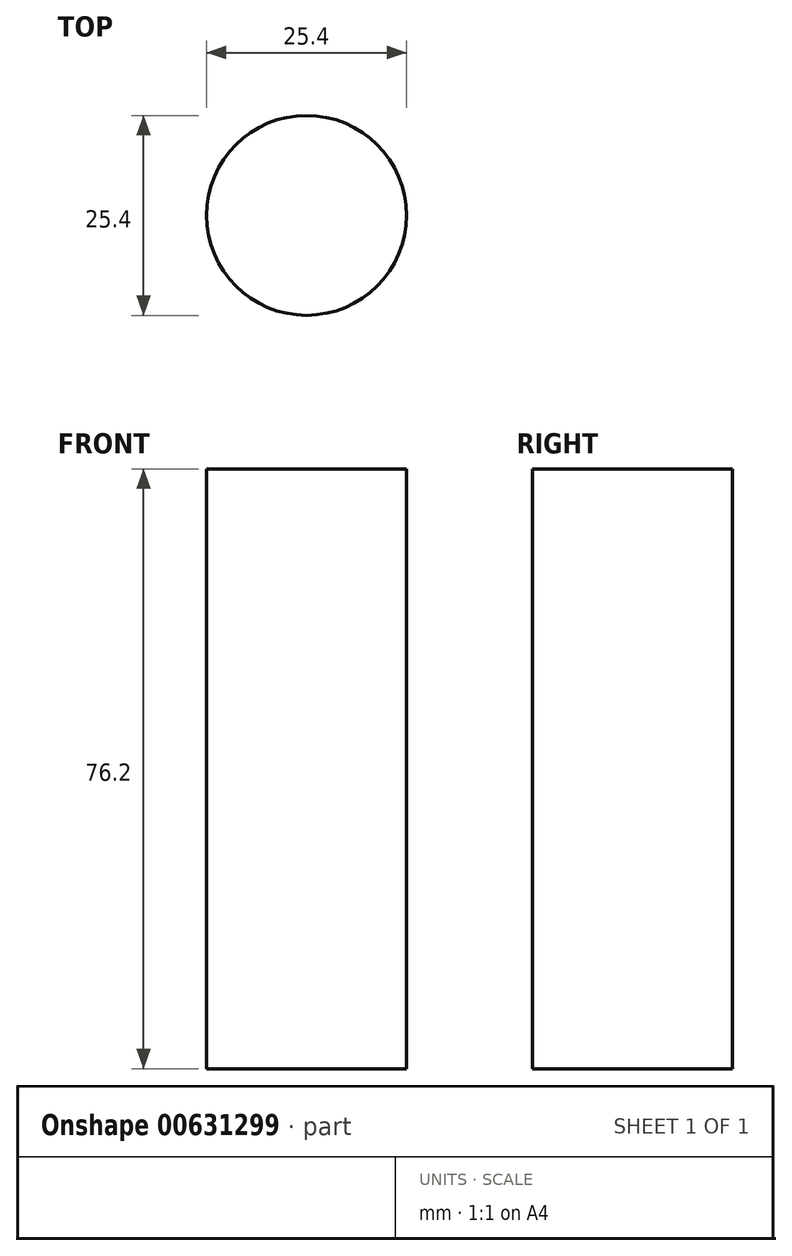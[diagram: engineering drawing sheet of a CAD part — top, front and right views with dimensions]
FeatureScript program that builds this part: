
annotation { "Feature Type Name" : "Feature", "Feature Type Description" : "" }
export const myFeature = defineFeature(function(context is Context, id is Id, definition is map)
    precondition{}
    {
        {
            var Q0;
            Q0=qCreatedBy(makeId("Front.planeOp"),FACE);
            var sketch = newSketch(context, id + "F0", { "sketchPlane" : qUnion([Q0])});
            skLineSegment(sketch, "E0.bottom", {"start": v(0, 0) * mm, "end": v(12.7, 0) * mm});
            skLineSegment(sketch, "E0.top", {"start": v(0, 76.2) * mm, "end": v(12.7, 76.2) * mm});
            skLineSegment(sketch, "E0.left", {"start": v(0, 0) * mm, "end": v(0, 76.2) * mm});
            skLineSegment(sketch, "E0.right", {"start": v(12.7, 0) * mm, "end": v(12.7, 76.2) * mm});
            skSolve(sketch);
        }
        {
            var Q0;
            Q0=makeQuery(id+"F0.imprint","IMPRINT",FACE,{"disambiguationData":[TD([[makeQuery(id+"F0.imprint","IMPRINT",EDGE,{"derivedFrom":sQuery(id+"F0.wireOp",EDGE,"E0.bottom")}),1.0]])]});
            var Q1;
            Q1=sQuery(id+"F0.wireOp",EDGE,"E0.left");
            revolve(context, id + "F1", {"entities" : qUnion([Q0]), "axis" : qUnion([Q1]), "revolveType" : RevolveType.FULL});
        }
    });
